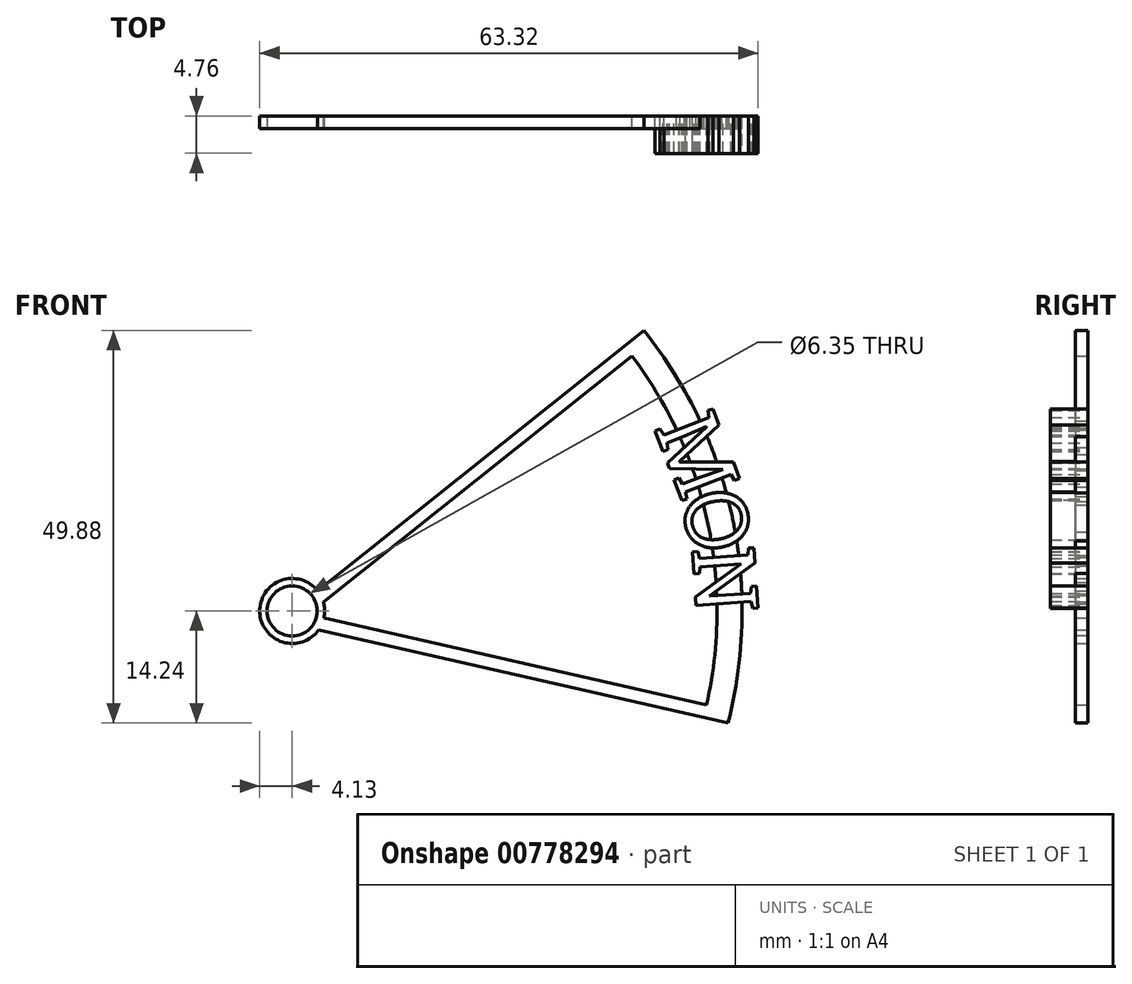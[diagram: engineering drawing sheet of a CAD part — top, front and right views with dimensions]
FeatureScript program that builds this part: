
annotation { "Feature Type Name" : "Feature", "Feature Type Description" : "" }
export const myFeature = defineFeature(function(context is Context, id is Id, definition is map)
    precondition{}
    {
        {
            var Q0;
            Q0=qCreatedBy(makeId("Front.planeOp"),FACE);
            var sketch = newSketch(context, id + "F0", { "sketchPlane" : qUnion([Q0])});
            skCircle(sketch, "E0", {"center": v(0, 0) * mm, "radius": 59.18 * mm, "construction": true});
            skCircle(sketch, "E1", {"center": v(0, 0) * mm, "radius": 50.8 * mm, "construction": true});
            skLineSegment(sketch, "E2", {"start": v(0, 0) * mm, "end": v(0, 59.18) * mm, "construction": true});
            skLineSegment(sketch, "E3", {"start": v(0, 0) * mm, "end": v(46.26, 36.9) * mm, "construction": true});
            skLineSegment(sketch, "E4", {"start": v(0, 0) * mm, "end": v(55.28, 21.14) * mm, "construction": true});
            skLineSegment(sketch, "E5", {"start": v(0, 0) * mm, "end": v(57.9, 12.24) * mm, "construction": true});
            skLineSegment(sketch, "E6", {"start": v(0, 0) * mm, "end": v(59.04, 4.06) * mm, "construction": true});
            skText(sketch, "E7", { "text": "M", "fontName": "RobotoSlab-Regular.ttf"});
            skText(sketch, "E8", { "text": "O", "fontName": "RobotoSlab-Regular.ttf"});
            skText(sketch, "E9", { "text": "N", "fontName": "RobotoSlab-Regular.ttf"});
            skLineSegment(sketch, "E10", {"start": v(0, 0) * mm, "end": v(53.39, 26.08) * mm, "construction": true});
            skLineSegment(sketch, "E11", {"start": v(0, 0) * mm, "end": v(59.34, -0.3) * mm, "construction": true});
            skLineSegment(sketch, "E12", {"start": v(0, 0) * mm, "end": v(57.7, -13.15) * mm, "construction": true});
            const initialGuessF0  = {"E7": [0.04598, 0.02324, 0.35727, -0.934, 0.00794], "E8": [0.0493, 0.01453, 0.20676, -0.9784, 0.00794], "E9": [0.05082, 0.00788, 0.06859, -0.99765, 0.00794]};
            skSetInitialGuess(sketch, initialGuessF0);
            skSolve(sketch);
        }
        {
            var Q0;
            Q0=qSketchRegion(id+"F0",true);
            extrude(context, id + "F1", {"entities" : qUnion([Q0]), "depth" : 4.76 * mm, "offsetDistance" : 25.4 * mm});
        }
        {
            var Q0;
            Q0=qCreatedBy(makeId("Front.planeOp"),FACE);
            var sketch = newSketch(context, id + "F2", { "sketchPlane" : qUnion([Q0])});
            skCircle(sketch, "E13", {"center": v(0, 0) * mm, "radius": 4.13 * mm, "construction": true});
            skCircle(sketch, "E14", {"center": v(0, 0) * mm, "radius": 57.15 * mm, "construction": true});
            skCircle(sketch, "E15", {"center": v(0, 0) * mm, "radius": 53.98 * mm, "construction": true});
            skLineSegment(sketch, "E16", {"start": v(0, 0) * mm, "end": v(0, 57.15) * mm, "construction": true});
            skLineSegment(sketch, "E17", {"start": v(44.68, 35.64) * mm, "end": v(0, 0) * mm, "construction": true});
            skLineSegment(sketch, "E18", {"start": v(43.17, 32.4) * mm, "end": v(3.97, 1.13) * mm, "construction": true});
            skLineSegment(sketch, "E19", {"start": v(55.35, -14.24) * mm, "end": v(3.36, -2.4) * mm, "construction": true});
            skCircle(sketch, "E20", {"center": v(0, 0) * mm, "radius": 4.13 * mm});
            skLineSegment(sketch, "E21", {"start": v(44.68, 35.64) * mm, "end": v(3.23, 2.57) * mm});
            skLineSegment(sketch, "E22", {"start": v(43.17, 32.4) * mm, "end": v(3.97, 1.13) * mm});
            skLineSegment(sketch, "E23", {"start": v(55.35, -14.24) * mm, "end": v(3.36, -2.4) * mm});
            skArc(sketch, "E24", {"start": v(55.35, -14.24) * mm, "mid": v(55.9, 11.96) * mm, "end": v(44.68, 35.64) * mm});
            skArc(sketch, "E25", {"start": v(52.63, -12) * mm, "mid": v(52.79, 11.25) * mm, "end": v(43.17, 32.4) * mm});
            skLineSegment(sketch, "E26", {"start": v(0.13, 0.03) * mm, "end": v(52.64, -11.94) * mm, "construction": true});
            skLineSegment(sketch, "E27", {"start": v(4.04, -0.86) * mm, "end": v(52.64, -11.94) * mm});
            skSolve(sketch);
        }
        {
            var Q0;
            {var subQ0=sQuery(id+"F2.wireOp",EDGE,"E21");Q0=makeQuery(id+"F2.imprint","IMPRINT",FACE,{"disambiguationData":[TD([[makeQuery(id+"F2.imprint","IMPRINT",EDGE,{"derivedFrom":subQ0}),1.0]])]});}
            var Q1;
            {var subQ0=sQuery(id+"F2.wireOp",EDGE,"E20");var subQ1=makeQuery(id+"F2.imprint","INTERSECT",VERTEX,{"derivedFrom":[subQ0,sQuery(id+"F2.wireOp",EDGE,"E21")]});Q1=makeQuery(id+"F2.imprint","IMPRINT",FACE,{"disambiguationData":[TD([[makeQuery(id+"F2.imprint","IMPRINT",EDGE,{"disambiguationData":[TD([[subQ1,1.0]])],"derivedFrom":subQ0}),1.0]])]});}
            extrude(context, id + "F3", {"entities" : qUnion([Q0, Q1]), "operationType" : NewBodyOperationType.ADD, "depth" : 1.59 * mm, "offsetDistance" : 25.4 * mm});
        }
        {
            var Q0;
            {var subQ0=sQuery(id+"F2.wireOp",EDGE,"E22");var subQ1=sQuery(id+"F2.wireOp",EDGE,"E20");var subQ2=sQuery(id+"F2.wireOp",EDGE,"E27");var subQ3=sQuery(id+"F2.wireOp",EDGE,"E21");var subQ4=sQuery(id+"F2.wireOp",EDGE,"E23");var subQ5=sQuery(id+"F2.wireOp",EDGE,"E24");var subQ6=sQuery(id+"F2.wireOp",EDGE,"E25");Q0=makeQuery(id+"F3.boolean.opBoolean","SPLIT",FACE,{"disambiguationData":[TD([makeQuery(id+"F1.opExtrude","SWEPT_FACE",FACE,{"disambiguationData":[OSD([sQuery(id+"F0.wireOp",EDGE,"E7.sketch_text.stroke-12")])]})])],"derivedFrom":makeQuery(id+"F3.opExtrude","CAP_FACE",FACE,{"disambiguationData":[OSD([subQ1,subQ3,subQ0,subQ4,subQ5,subQ6,subQ2])],"isStart":false})});}
            var sketch = newSketch(context, id + "F4", { "sketchPlane" : qUnion([Q0])});
            skPoint(sketch, "E28", {"position": v(0, 0) * mm});
            skSolve(sketch);
        }
        {
            var Q0;
            Q0=sQuery(id+"F4.wireOp",VERTEX,"E28");
            var Q1;
            Q1=makeQuery(id+"F1.opExtrude","SWEPT_BODY",BODY,{"disambiguationData":[OSD([sQuery(id+"F0.wireOp",EDGE,"E7.sketch_text.stroke-0"),sQuery(id+"F0.wireOp",EDGE,"E7.sketch_text.stroke-1"),sQuery(id+"F0.wireOp",EDGE,"E7.sketch_text.stroke-2"),sQuery(id+"F0.wireOp",EDGE,"E7.sketch_text.stroke-3"),sQuery(id+"F0.wireOp",EDGE,"E7.sketch_text.stroke-4"),sQuery(id+"F0.wireOp",EDGE,"E7.sketch_text.stroke-5"),sQuery(id+"F0.wireOp",EDGE,"E7.sketch_text.stroke-6"),sQuery(id+"F0.wireOp",EDGE,"E7.sketch_text.stroke-7"),sQuery(id+"F0.wireOp",EDGE,"E7.sketch_text.stroke-8"),sQuery(id+"F0.wireOp",EDGE,"E7.sketch_text.stroke-9"),sQuery(id+"F0.wireOp",EDGE,"E7.sketch_text.stroke-10"),sQuery(id+"F0.wireOp",EDGE,"E7.sketch_text.stroke-11"),sQuery(id+"F0.wireOp",EDGE,"E7.sketch_text.stroke-12"),sQuery(id+"F0.wireOp",EDGE,"E7.sketch_text.stroke-13"),sQuery(id+"F0.wireOp",EDGE,"E7.sketch_text.stroke-14"),sQuery(id+"F0.wireOp",EDGE,"E7.sketch_text.stroke-15"),sQuery(id+"F0.wireOp",EDGE,"E7.sketch_text.stroke-16"),sQuery(id+"F0.wireOp",EDGE,"E7.sketch_text.stroke-17"),sQuery(id+"F0.wireOp",EDGE,"E7.sketch_text.stroke-18"),sQuery(id+"F0.wireOp",EDGE,"E7.sketch_text.stroke-19"),sQuery(id+"F0.wireOp",EDGE,"E7.sketch_text.stroke-20"),sQuery(id+"F0.wireOp",EDGE,"E7.sketch_text.stroke-21"),sQuery(id+"F0.wireOp",EDGE,"E7.sketch_text.stroke-22"),sQuery(id+"F0.wireOp",EDGE,"E7.sketch_text.stroke-23"),sQuery(id+"F0.wireOp",EDGE,"E7.sketch_text.stroke-24"),sQuery(id+"F0.wireOp",EDGE,"E7.sketch_text.stroke-25"),sQuery(id+"F0.wireOp",EDGE,"E7.sketch_text.stroke-26"),sQuery(id+"F0.wireOp",EDGE,"E7.sketch_text.stroke-27"),sQuery(id+"F0.wireOp",EDGE,"E7.sketch_text.stroke-28"),sQuery(id+"F0.wireOp",EDGE,"E7.sketch_text.stroke-29"),sQuery(id+"F0.wireOp",EDGE,"E7.sketch_text.stroke-30")])]});
            hole(context, id + "F5", {"style" : HoleStyle.SIMPLE, "endStyle" : HoleEndStyle.THROUGH, "holeDiameter" : 6.35 * mm, "majorDiameter" : 6.35 * mm, "isTappedThrough" : true, "tappedDepth" : 12.7 * mm, "tapClearance" : 3, "locations" : qUnion([Q0]), "scope" : qUnion([Q1])});
        }
    });
